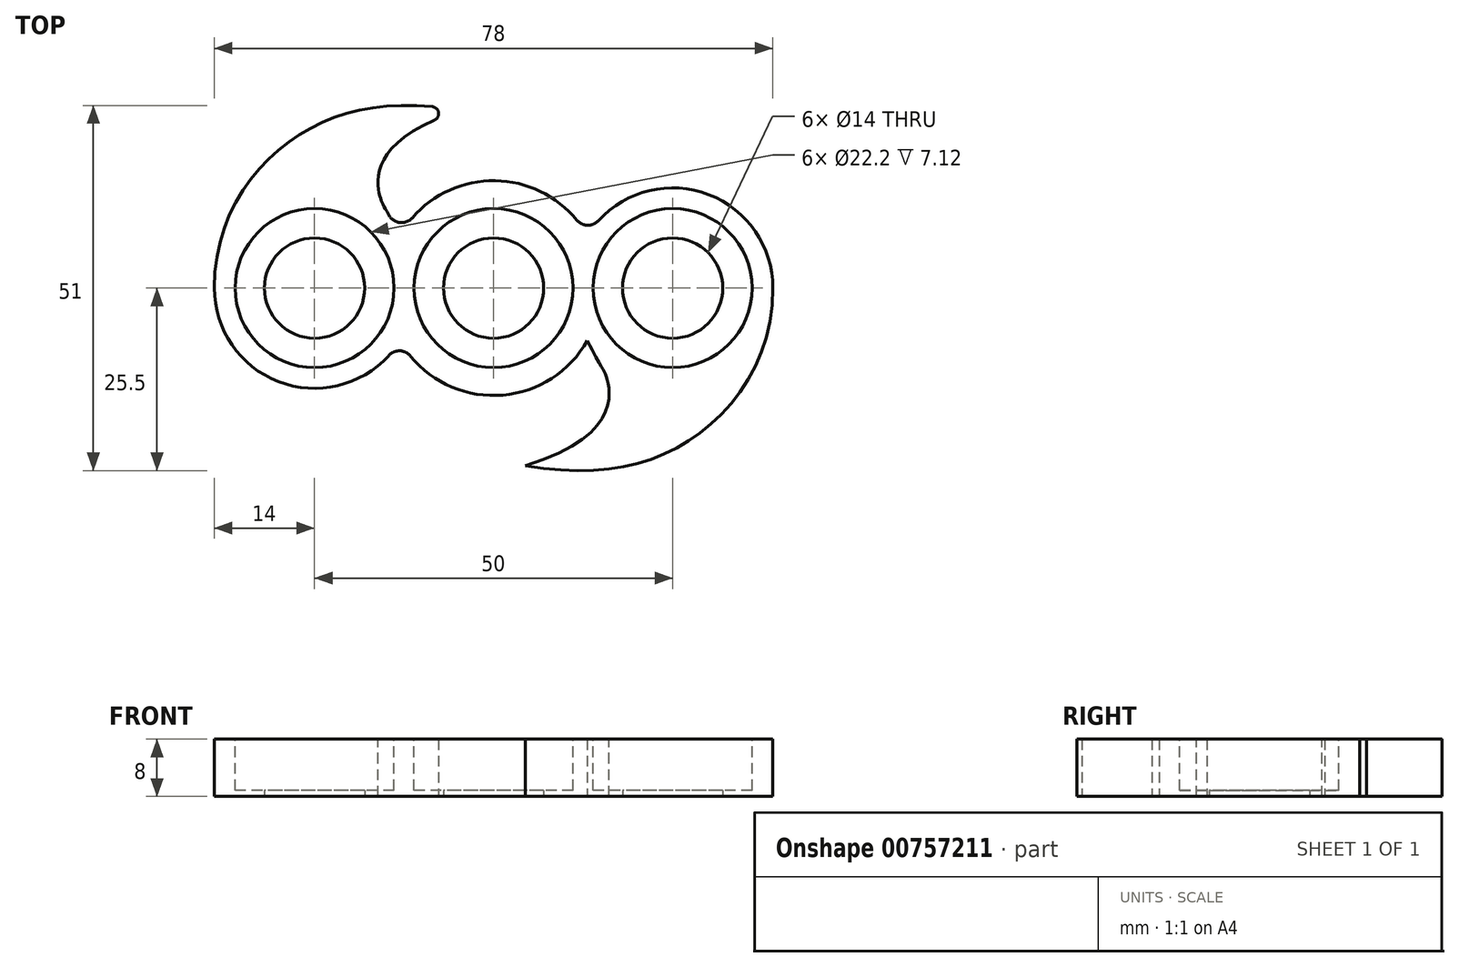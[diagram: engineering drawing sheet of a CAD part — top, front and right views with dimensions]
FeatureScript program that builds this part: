
annotation { "Feature Type Name" : "Feature", "Feature Type Description" : "" }
export const myFeature = defineFeature(function(context is Context, id is Id, definition is map)
    precondition{}
    {
        {
            var Q0;
            Q0=qCreatedBy(makeId("Top.planeOp"),FACE);
            var sketch = newSketch(context, id + "F0", { "sketchPlane" : qUnion([Q0])});
            skCircle(sketch, "E0", {"center": v(0, 0) * mm, "radius": 11 * mm, "construction": true});
            skCircle(sketch, "E1", {"center": v(0, 0) * mm, "radius": 15 * mm});
            skLineSegment(sketch, "E2", {"start": v(0, 0) * mm, "end": v(-25, 0) * mm, "construction": true});
            skCircle(sketch, "E3", {"center": v(-25, 0) * mm, "radius": 11 * mm, "construction": true});
            skCircle(sketch, "E4", {"center": v(-25, 0) * mm, "radius": 14 * mm});
            skFitSpline(sketch, "E5", {"points": [v(-39, 0) * mm, v(-28.17, 20.7) * mm, v(-4.46, 24.8) * mm], "startDerivative": vector(0, 56.31) * mm, "endDerivative": vector(59.36, -10.34) * mm});
            skFitSpline(sketch, "E6", {"points": [v(-4.46, 24.8) * mm, v(-15.8, 12.6) * mm, v(-13.08, 7.34) * mm], "startDerivative": vector(-62.8, -18.84) * mm, "endDerivative": vector(17.56, -33.85) * mm});
            skLineSegment(sketch, "E7", {"start": v(0, 0) * mm, "end": v(0, 0) * mm});
            skLineSegment(sketch, "E8", {"start": v(0, 0) * mm, "end": v(38.66, 38.66) * mm, "construction": true});
            skCircle(sketch, "E9.MirrorC", {"center": v(25, 0) * mm, "radius": 14 * mm});
            skCircle(sketch, "E10.MirrorC", {"center": v(25, 0) * mm, "radius": 11 * mm, "construction": true});
            skLineSegment(sketch, "E11", {"start": v(0, 36.93) * mm, "end": v(0, 0) * mm, "construction": true});
            skCircle(sketch, "E12", {"center": v(-25, 0) * mm, "radius": 7 * mm});
            skCircle(sketch, "E13", {"center": v(0, 0) * mm, "radius": 7 * mm});
            skCircle(sketch, "E14", {"center": v(25, 0) * mm, "radius": 7 * mm});
            skLineSegment(sketch, "E15.MirrorCS", {"start": v(0, 0) * mm, "end": v(38.66, -38.66) * mm, "construction": true});
            skFitSpline(sketch, "E16.MirrorCS", {"points": [v(4.46, -24.8) * mm, v(15.8, -12.6) * mm, v(13.08, -7.34) * mm], "startDerivative": vector(62.8, 18.84) * mm, "endDerivative": vector(-17.56, 33.85) * mm});
            skFitSpline(sketch, "E17.MirrorCS", {"points": [v(39, 0) * mm, v(28.17, -20.7) * mm, v(4.46, -24.8) * mm], "startDerivative": vector(0, -56.31) * mm, "endDerivative": vector(-59.36, 10.34) * mm});
            skFitSpline(sketch, "E18.MirrorCS", {"points": [v(4.46, -24.8) * mm, v(15.8, -12.6) * mm, v(13.08, -7.34) * mm], "startDerivative": vector(62.8, 18.84) * mm, "endDerivative": vector(-17.56, 33.85) * mm});
            skFitSpline(sketch, "E19.MirrorCS", {"points": [v(39, 0) * mm, v(28.17, -20.7) * mm, v(4.46, -24.8) * mm], "startDerivative": vector(0, -56.31) * mm, "endDerivative": vector(-59.36, 10.34) * mm});
            skSolve(sketch);
        }
        {
            var Q0;
            Q0=qSketchRegion(id+"F0",true);
            extrude(context, id + "F1", {"entities" : qUnion([Q0]), "depth" : 8 * mm, "offsetDistance" : 25 * mm});
        }
        {
            var Q0;
            Q0=makeQuery(id+"F1.opExtrude","CAP_FACE",FACE,{"disambiguationData":[OSD([sQuery(id+"F0.wireOp",EDGE,"E1"),sQuery(id+"F0.wireOp",EDGE,"E4"),sQuery(id+"F0.wireOp",EDGE,"E5"),sQuery(id+"F0.wireOp",EDGE,"E6"),sQuery(id+"F0.wireOp",EDGE,"E9.MirrorC"),sQuery(id+"F0.wireOp",EDGE,"5fff56f5-4cb7-41f4-b0d8-fc3094ce9e850.MirrorCS"),sQuery(id+"F0.wireOp",EDGE,"8e6b7095-6aad-4670-bd88-e956415897bd0.MirrorCS"),sQuery(id+"F0.wireOp",EDGE,"7d13797c-2248-4f8d-801f-307ed402d1c3"),sQuery(id+"F0.wireOp",EDGE,"bb3e0d30-0f37-45a4-8635-daa02c4d00310.MirrorCS"),sQuery(id+"F0.wireOp",EDGE,"E12"),sQuery(id+"F0.wireOp",EDGE,"E13"),sQuery(id+"F0.wireOp",EDGE,"E14")])],"isStart":false});
            var sketch = newSketch(context, id + "F2", { "sketchPlane" : qUnion([Q0])});
            skCircle(sketch, "E20", {"center": v(-25, 0) * mm, "radius": 11.1 * mm});
            skCircle(sketch, "E21", {"center": v(0, 0) * mm, "radius": 11.1 * mm});
            skCircle(sketch, "E22", {"center": v(25, 0) * mm, "radius": 11.1 * mm});
            skSolve(sketch);
        }
        {
            var Q0;
            Q0=qSketchRegion(id+"F2",true);
            extrude(context, id + "F3", {"entities" : qUnion([Q0]), "operationType" : NewBodyOperationType.REMOVE, "oppositeDirection" : true, "depth" : 7.12 * mm, "offsetDistance" : 25 * mm});
        }
        {
            var Q0;
            Q0=makeQuery(id+"F1.opExtrude","SWEPT_EDGE",EDGE,{"disambiguationData":[OSD([sQuery(id+"F0.wireOp",EDGE,"E1"),sQuery(id+"F0.wireOp",EDGE,"E4"),sQuery(id+"F0.wireOp",EDGE,"E6")])]});
            var Q1;
            Q1=makeQuery(id+"F1.opExtrude","SWEPT_EDGE",EDGE,{"disambiguationData":[OSD([sQuery(id+"F0.wireOp",EDGE,"E1"),sQuery(id+"F0.wireOp",EDGE,"E9.MirrorC")])]});
            var Q2;
            Q2=makeQuery(id+"F1.opExtrude","SWEPT_EDGE",EDGE,{"disambiguationData":[OSD([sQuery(id+"F0.wireOp",EDGE,"E1"),sQuery(id+"F0.wireOp",EDGE,"E4")])]});
            var Q3;
            Q3=makeQuery(id+"F1.opExtrude","SWEPT_EDGE",EDGE,{"disambiguationData":[OSD([sQuery(id+"F0.wireOp",EDGE,"E1"),sQuery(id+"F0.wireOp",EDGE,"E9.MirrorC"),sQuery(id+"F0.wireOp",EDGE,"E18.MirrorCS")])]});
            fillet(context, id + "F4", {"entities" : qUnion([Q0, Q1, Q2, Q3]), "radius" : 2 * mm, "tangentPropagation" : true, "allowEdgeOverflow" : false});
        }
        {
            var Q0;
            Q0=makeQuery(id+"F1.opExtrude","SWEPT_EDGE",EDGE,{"disambiguationData":[OSD([sQuery(id+"F0.wireOp",EDGE,"E5"),sQuery(id+"F0.wireOp",EDGE,"E6")])]});
            var Q1;
            Q1=makeQuery(id+"F1.opExtrude","SWEPT_EDGE",EDGE,{"disambiguationData":[OSD([sQuery(id+"F0.wireOp",EDGE,"E18.MirrorCS"),sQuery(id+"F0.wireOp",EDGE,"E19.MirrorCS")])]});
            fillet(context, id + "F5", {"entities" : qUnion([Q0, Q1]), "radius" : 1 * mm, "tangentPropagation" : true, "allowEdgeOverflow" : false});
        }
    });
